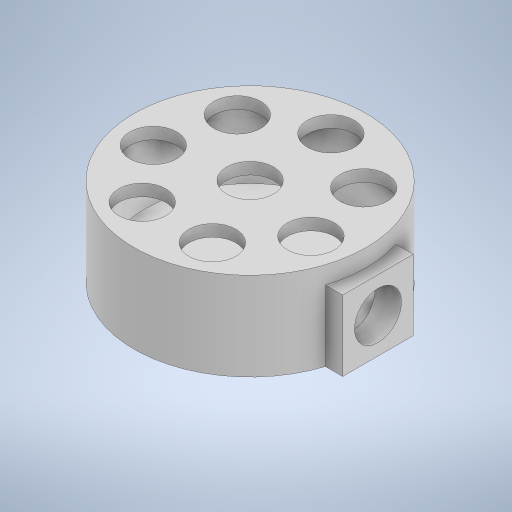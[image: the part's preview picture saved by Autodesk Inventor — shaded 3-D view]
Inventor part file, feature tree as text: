
AUTODESK INVENTOR PART (.ipt)
format: ipt  version: 2024 (Build 280153000, 153)  size: 323,072 bytes
history: native  units: mm
features: extrude x7, sketch x4, other x3, projected_geometry x2
ambient origin geometry x8: Origin, YZ Plane, XZ Plane, XY Plane, X Axis, Y Axis, Z Axis, Center Point
bodies: Body1 (feature_tree)
feature tree (16):
  other  "솔리드1"
  sketch  "스케치1"
  extrude  "돌출1"  Depth=11.0mm
  extrude  "돌출2"  Depth=3.2mm
  other  "작업 평면1"
  sketch  "스케치2"
  extrude  "돌출3"  Depth=70.0mm TaperAngle=360.0deg
  other  "작업 평면3"
  extrude  "돌출4"  Depth=15.8mm
  extrude  "돌출5"  Depth=3.2mm
  extrude  "돌출6"  Depth=6.0mm TaperAngle=0.0deg
  extrude  "돌출7"  Depth=5.2mm TaperAngle=0.0deg
  projected_geometry  "투영된 루프1"
  sketch  "스케치5"
  projected_geometry  "투영된 루프2"
  sketch  "스케치7"
